# Revit family: ALUMIDI
name_source: partatom
category: Connessioni strutturali
revit_build: Autodesk Revit 2016 (Build: 20151007_0715(x64)
units: mm (PartAtom-declared; Revit-internal decimal feet)

## family parameters
Attiva taglio nelle viste = No
Condiviso = No
Host = Superficie
Materiale per comportamento modello = Altro
Numero OmniClass = 23.20.40.11.24.14
Taglio con vuoti quando caricato = Sì
Titolo OmniClass = Wood Connectors

## types (9) — shared parameters
Catalogo = Piastre e connettori per legno
Family Version = 1.0.0
Fori ala cemento diametro = 9 mm  [stored 0.0295276 ft]
Fori ala legno diametro = 5 mm  [stored 0.0164042 ft]
Larghezza ala = 80 mm  [stored 0.262467 ft]
Lunghezza anima = 109.4 mm  [stored 0.358924 ft]
Materiale = <Per categoria>
Produttore = Rotho Blaas srl
Spessore = 6 mm  [stored 0.019685 ft]
Tipo famiglia = Alumidi 80 : Tipo
URL = http://www.rothoblaas.com
zero-valued in all types: Prospetto di default

## per-type parameters (varying)
| type | Altezza |
| ALUMIDI 240 | 240 mm  [stored 0.787402 ft] |
| ALUMIDI 200 | 200 mm  [stored 0.656168 ft] |
| ALUMIDI 160 | 160 mm  [stored 0.524934 ft] |
| ALUMIDI   80 | 80 mm  [stored 0.262467 ft] |
| ALUMIDI 120 | 120 mm  [stored 0.393701 ft] |
| ALUMIDI 280 (da verga ALUMIDI2200) | 280 mm  [stored 0.918635 ft] |
| ALUMIDI 320 (da verga ALUMIDI2200) | 320 mm  [stored 1.04987 ft] |
| ALUMIDI 360 (da verga ALUMIDI2200) | 360 mm  [stored 1.1811 ft] |
| ALUMIDI 400 (da verga ALUMIDI2200) | 400 mm  [stored 1.31234 ft] |

note: [stored X ft] marks values corroborated as IEEE doubles in the binary element streams (Revit-internal decimal feet)
